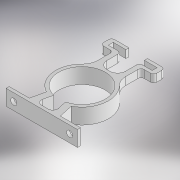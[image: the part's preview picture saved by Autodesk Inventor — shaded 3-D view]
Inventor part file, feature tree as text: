
AUTODESK INVENTOR PART (.ipt)
format: ipt  version: 2018.2 (Build 222227000, 227)  size: 221,696 bytes
history: native  units: mm
features: extrude x3, sketch x3, projected_geometry x2, fillet x1, mirror x1
ambient origin geometry x8: Origin, YZ Plane, XZ Plane, XY Plane, X Axis, Y Axis, Z Axis, Center Point
bodies: Solid1 (feature_tree)
feature tree (10):
  extrude  "Extrusion1"  Depth=2.0mm
  extrude  "Extrusion2"  Depth=23.0mm
  extrude  "Extrusion3"  Depth=10.0mm
  fillet  "Fillet1"  Radius=2.0mm
  mirror  "Mirror1"
  sketch  "Sketch1"  dims[d0=26.0mm d1=2.0mm]
  sketch  "Sketch2"  dims[d2=18.0mm d3=23.0mm]
  projected_geometry  "Projected Loop1"
  projected_geometry  "Projected Loop2"
  sketch  "Sketch3"  dims[d4=8.0mm d6=8.0mm d7=2.0mm d8=15.0mm d9=3.0mm d10=4.0mm d11=10.0mm d12=0.0mm d13=36.0mm d14=4.0mm d15=4.0mm d16=10.0mm d17=0.0mm d18=3.2mm d19=14.15mm d20=3.0mm d21=2.0mm d22=2.0mm d23=3.0mm d24=6.0mm d25=31.0mm d26=5.0mm d27=0.0mm d28=2.0mm d29=5.0mm d30=10.0mm]
